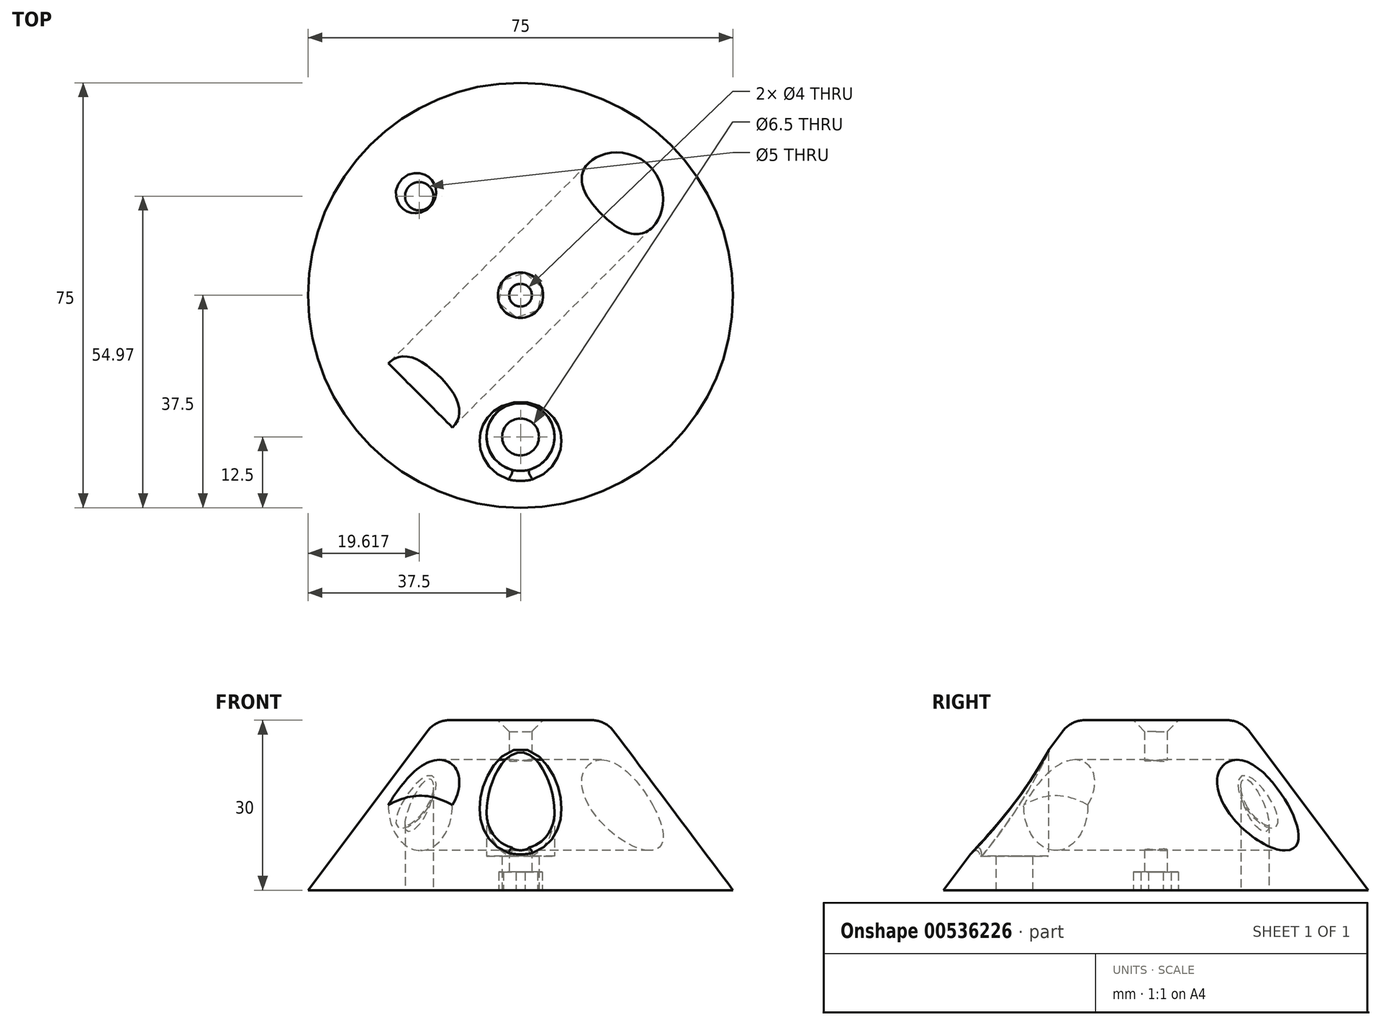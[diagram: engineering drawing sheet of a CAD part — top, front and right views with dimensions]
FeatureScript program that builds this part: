
annotation { "Feature Type Name" : "Feature", "Feature Type Description" : "" }
export const myFeature = defineFeature(function(context is Context, id is Id, definition is map)
    precondition{}
    {
        {
            var Q0;
            Q0=qCreatedBy(makeId("Front.planeOp"),FACE);
            var Q1;
            Q1=qCreatedBy(makeId("Right.planeOp"),FACE);
            cPlane(context, id + "F0", {"entities" : qUnion([Q0, Q1]), "cplaneType" : CPlaneType.MID_PLANE, "offset" : 25 * mm, "flipAlignment" : true, "width" : 150 * mm, "height" : 150 * mm});
        }
        {
            assignVariable(context, id + "F1", {"name" : "m6tiefe", "anyValue" : 6});
        }
        {
            var Q0;
            Q0=qCreatedBy(makeId("Top.planeOp"),FACE);
            var sketch = newSketch(context, id + "F2", { "sketchPlane" : qUnion([Q0])});
            skCircle(sketch, "E0", {"center": v(0, 0) * mm, "radius": 37.5 * mm});
            skSolve(sketch);
        }
        {
            var Q0;
            Q0=qCreatedBy(makeId("Top.planeOp"),FACE);
            cPlane(context, id + "F3", {"entities" : qUnion([Q0]), "cplaneType" : CPlaneType.OFFSET, "offset" : 30 * mm, "width" : 150 * mm, "height" : 150 * mm});
        }
        {
            var Q0;
            Q0=qCreatedBy(id+"F3.planeOp",FACE);
            var sketch = newSketch(context, id + "F4", { "sketchPlane" : qUnion([Q0])});
            skCircle(sketch, "E1", {"center": v(0, 0) * mm, "radius": 15 * mm});
            skSolve(sketch);
        }
        {
            var Q0;
            Q0=makeQuery(id+"F4.imprint","IMPRINT",FACE,{"disambiguationData":[TD([[makeQuery(id+"F4.imprint","IMPRINT",EDGE,{"derivedFrom":sQuery(id+"F4.wireOp",EDGE,"E1")}),1.0]])]});
            var Q1;
            Q1=makeQuery(id+"F2.imprint","IMPRINT",FACE,{"disambiguationData":[TD([[makeQuery(id+"F2.imprint","IMPRINT",EDGE,{"derivedFrom":sQuery(id+"F2.wireOp",EDGE,"E0")}),1.0]])]});
            loft(context, id + "F5", {"sheetProfilesArray" : [{ "sheetProfileEntities" : qUnion([Q0]) }, { "sheetProfileEntities" : qUnion([Q1]) }]});
        }
        {
            var Q0;
            Q0=makeQuery(id+"F2.imprint","IMPRINT",FACE,{"disambiguationData":[TD([[makeQuery(id+"F2.imprint","IMPRINT",EDGE,{"derivedFrom":sQuery(id+"F2.wireOp",EDGE,"E0")}),1.0]])]});
            var sketch = newSketch(context, id + "F6", { "sketchPlane" : qUnion([Q0])});
            skCircle(sketch, "E2", {"center": v(0, -25) * mm, "radius": 3.25 * mm});
            skSolve(sketch);
        }
        {
            var Q0;
            Q0=qSketchRegion(id+"F6",true);
            extrude(context, id + "F7", {"entities" : qUnion([Q0]), "operationType" : NewBodyOperationType.REMOVE, "endBound" : BoundingType.THROUGH_ALL, "depth" : 2 * (getVariable(context, 'm6tiefe')) * mm});
        }
        {
            var Q0;
            Q0=qCreatedBy(makeId("Top.planeOp"),FACE);
            cPlane(context, id + "F8", {"entities" : qUnion([Q0]), "cplaneType" : CPlaneType.OFFSET, "offset" : (getVariable(context, 'm6tiefe')) * mm, "width" : 150 * mm, "height" : 150 * mm});
        }
        {
            var Q0;
            Q0=qCreatedBy(id+"F8.planeOp",FACE);
            var sketch = newSketch(context, id + "F9", { "sketchPlane" : qUnion([Q0])});
            skCircle(sketch, "E3", {"center": v(0, -25) * mm, "radius": 6 * mm});
            skSolve(sketch);
        }
        {
            var Q0;
            Q0=qSketchRegion(id+"F9",true);
            extrude(context, id + "F10", {"entities" : qUnion([Q0]), "operationType" : NewBodyOperationType.REMOVE, "depth" : 25 * mm});
        }
        {
            var Q0;
            Q0=makeQuery(id+"F10.boolean.opBoolean","INTERSECT",EDGE,{"derivedFrom":[makeQuery(id+"F5.opLoft","SWEPT_FACE",FACE,{"disambiguationData":[OSD([sQuery(id+"F2.wireOp",EDGE,"E0"),sQuery(id+"F4.wireOp",EDGE,"E1")])]}),makeQuery(id+"F10.opExtrude","SWEPT_FACE",FACE,{"disambiguationData":[OSD([sQuery(id+"F9.wireOp",EDGE,"E3")])]})]});
            fillet(context, id + "F11", {"entities" : qUnion([Q0]), "radius" : 1 * mm, "tangentPropagation" : true, "rho" : 0.5, "crossSection" : FilletCrossSection.CONIC, "allowEdgeOverflow" : false});
        }
        {
            var Q0;
            Q0=qCreatedBy(id+"F0.planeOp",FACE);
            cPlane(context, id + "F12", {"entities" : qUnion([Q0]), "cplaneType" : CPlaneType.OFFSET, "offset" : 8 * mm, "width" : 150 * mm, "height" : 150 * mm});
        }
        {
            var Q0;
            Q0=makeQuery(id+"F2.imprint","IMPRINT",FACE,{"disambiguationData":[TD([[makeQuery(id+"F2.imprint","IMPRINT",EDGE,{"derivedFrom":sQuery(id+"F2.wireOp",EDGE,"E0")}),1.0]])]});
            var sketch = newSketch(context, id + "F13", { "sketchPlane" : qUnion([Q0])});
            skLineSegment(sketch, "E4", {"start": v(0, 0) * mm, "end": v(-26.47, 25.86) * mm, "construction": true});
            skCircle(sketch, "E5", {"center": v(0, 0) * mm, "radius": 25 * mm, "construction": true});
            skLineSegment(sketch, "E6", {"start": v(-25, 0) * mm, "end": v(0, 25.6) * mm, "construction": true});
            skCircle(sketch, "E7", {"center": v(-17.88, 17.47) * mm, "radius": 2.5 * mm});
            skSolve(sketch);
        }
        {
            var Q0;
            Q0=makeQuery(id+"F13.imprint","IMPRINT",FACE,{"disambiguationData":[TD([[makeQuery(id+"F13.imprint","IMPRINT",EDGE,{"derivedFrom":sQuery(id+"F13.wireOp",EDGE,"E7")}),1.0]])]});
            extrude(context, id + "F14", {"entities" : qUnion([Q0]), "operationType" : NewBodyOperationType.REMOVE, "endBound" : BoundingType.THROUGH_ALL, "depth" : 25 * mm});
        }
        {
            var Q0;
            Q0=makeQuery(id+"F14.boolean.opBoolean","INTERSECT",EDGE,{"derivedFrom":[makeQuery(id+"F5.opLoft","SWEPT_FACE",FACE,{"disambiguationData":[OSD([sQuery(id+"F2.wireOp",EDGE,"E0"),sQuery(id+"F4.wireOp",EDGE,"E1")])]}),makeQuery(id+"F14.opExtrude","SWEPT_FACE",FACE,{"disambiguationData":[OSD([sQuery(id+"F13.wireOp",EDGE,"E7")])]})]});
            fillet(context, id + "F15", {"entities" : qUnion([Q0]), "radius" : 1 * mm, "tangentPropagation" : true, "allowEdgeOverflow" : false});
        }
        {
            var Q0;
            Q0=qCreatedBy(makeId("Front.planeOp"),FACE);
            var Q1;
            Q1=qCreatedBy(makeId("Right.planeOp"),FACE);
            cPlane(context, id + "F16", {"entities" : qUnion([Q0, Q1]), "cplaneType" : CPlaneType.MID_PLANE, "offset" : 25 * mm, "width" : 150 * mm, "height" : 150 * mm});
        }
        {
            var Q0;
            Q0=qCreatedBy(id+"F16.planeOp",FACE);
            var sketch = newSketch(context, id + "F17", { "sketchPlane" : qUnion([Q0])});
            skLineSegment(sketch, "E8", {"start": v(0, 0) * mm, "end": v(0, 15) * mm, "construction": true});
            skCircle(sketch, "E9", {"center": v(0, 15) * mm, "radius": 8 * mm});
            skSolve(sketch);
        }
        {
            var Q0;
            Q0=makeQuery(id+"F17.imprint","IMPRINT",FACE,{"disambiguationData":[TD([[makeQuery(id+"F17.imprint","IMPRINT",EDGE,{"derivedFrom":sQuery(id+"F17.wireOp",EDGE,"E9")}),1.0]])]});
            extrude(context, id + "F18", {"entities" : qUnion([Q0]), "operationType" : NewBodyOperationType.REMOVE, "endBound" : BoundingType.THROUGH_ALL, "oppositeDirection" : true, "depth" : 100 * mm, "offsetDistance" : 25 * mm});
        }
        {
            var Q0;
            Q0=makeQuery(id+"F18.boolean.opBoolean","COPY",FACE,{"derivedFrom":makeQuery(id+"F18.opExtrude","CAP_FACE",FACE,{"disambiguationData":[OSD([sQuery(id+"F17.wireOp",EDGE,"E9")])],"isStart":true})});
            extrude(context, id + "F19", {"entities" : qUnion([Q0]), "operationType" : NewBodyOperationType.REMOVE, "oppositeDirection" : true, "depth" : 25 * mm, "offsetDistance" : 25 * mm});
        }
        {
            var Q0;
            Q0=makeQuery(id+"F2.imprint","IMPRINT",FACE,{"disambiguationData":[TD([[makeQuery(id+"F2.imprint","IMPRINT",EDGE,{"derivedFrom":sQuery(id+"F2.wireOp",EDGE,"E0")}),1.0]])]});
            var sketch = newSketch(context, id + "F20", { "sketchPlane" : qUnion([Q0])});
            skCircle(sketch, "E10.cCircle", {"center": v(0, 0) * mm, "radius": 3.5 * mm, "construction": true});
            skLineSegment(sketch, "E10.0", {"start": v(3.04, -2.66) * mm, "end": v(-0.79, -3.96) * mm});
            skLineSegment(sketch, "E10.1", {"start": v(-0.79, -3.96) * mm, "end": v(-3.83, -1.3) * mm});
            skLineSegment(sketch, "E10.2", {"start": v(-3.83, -1.3) * mm, "end": v(-3.04, 2.66) * mm});
            skLineSegment(sketch, "E10.3", {"start": v(-3.04, 2.66) * mm, "end": v(0.79, 3.96) * mm});
            skLineSegment(sketch, "E10.4", {"start": v(0.79, 3.96) * mm, "end": v(3.83, 1.3) * mm});
            skLineSegment(sketch, "E10.5", {"start": v(3.83, 1.3) * mm, "end": v(3.04, -2.66) * mm});
            skPoint(sketch, "E10.0.midPoint", {"position": v(1.13, -3.31) * mm});
            skLineSegment(sketch, "E11", {"start": v(3.04, -2.66) * mm, "end": v(0.79, 3.96) * mm, "construction": true});
            skCircle(sketch, "E12", {"center": v(0, 0) * mm, "radius": 2 * mm});
            skSolve(sketch);
        }
        {
            var Q0;
            Q0=makeQuery(id+"F20.imprint","IMPRINT",FACE,{"disambiguationData":[TD([[makeQuery(id+"F20.imprint","IMPRINT",EDGE,{"derivedFrom":sQuery(id+"F20.wireOp",EDGE,"E10.0")}),-1.0]])]});
            extrude(context, id + "F21", {"entities" : qUnion([Q0]), "operationType" : NewBodyOperationType.REMOVE, "depth" : 3.2 * mm, "offsetDistance" : 25 * mm});
        }
        {
            var Q0;
            Q0=makeQuery(id+"F20.imprint","IMPRINT",FACE,{"disambiguationData":[TD([[makeQuery(id+"F20.imprint","IMPRINT",EDGE,{"derivedFrom":sQuery(id+"F20.wireOp",EDGE,"E12")}),1.0]])]});
            extrude(context, id + "F22", {"entities" : qUnion([Q0]), "operationType" : NewBodyOperationType.REMOVE, "endBound" : BoundingType.THROUGH_ALL, "depth" : 25 * mm, "offsetDistance" : 25 * mm});
        }
        {
            var Q0;
            Q0=makeQuery(id+"F22.boolean.opBoolean","INTERSECT",EDGE,{"derivedFrom":[makeQuery(id+"F5.opLoft","CAP_FACE",FACE,{"disambiguationData":[OSD([makeQuery(id+"F4.imprint","IMPRINT",FACE,{"disambiguationData":[TD([[makeQuery(id+"F4.imprint","IMPRINT",EDGE,{"derivedFrom":sQuery(id+"F4.wireOp",EDGE,"E1")}),1.0]])]})])],"isStart":true}),makeQuery(id+"F22.opExtrude","SWEPT_FACE",FACE,{"disambiguationData":[OSD([sQuery(id+"F20.wireOp",EDGE,"E12")])]})]});
            chamfer(context, id + "F23", {"entities" : qUnion([Q0]), "width" : 2 * mm, "tangentPropagation" : true});
        }
        {
            var Q0;
            Q0=makeQuery(id+"F5.opLoft","MID_CAP_EDGE",EDGE,{"disambiguationData":[OSD([sQuery(id+"F4.wireOp",EDGE,"E1")])],"capPos":0.0});
            fillet(context, id + "F24", {"entities" : qUnion([Q0]), "radius" : 5 * mm, "tangentPropagation" : true, "allowEdgeOverflow" : false});
        }
    });
